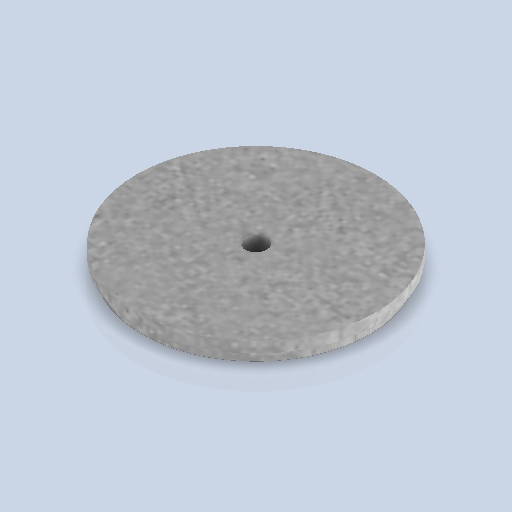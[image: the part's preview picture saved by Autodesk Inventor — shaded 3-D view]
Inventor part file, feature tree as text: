
AUTODESK INVENTOR PART (.ipt)
format: ipt  version: 2024.2 (Build 282272000, 272)  size: 238,592 bytes
history: native  units: mm
features: sketch x2, revolve x1, extrude x1
ambient origin geometry x8: Origin, YZ Plane, XZ Plane, XY Plane, X Axis, Y Axis, Z Axis, Center Point
bodies: Volumenkörper1 (feature_tree)
feature tree (4):
  revolve  "Umdrehung1"
  extrude  "Extrusion1"  Depth=3.0mm
  sketch  "Skizze1"  dims[d0=3.0mm d1=3.0mm]
  sketch  "Skizze2"  dims[d2=63.0mm d3=66.0mm d4=90.0deg d5=6.0mm d6=10.0mm d7=0.0mm]
